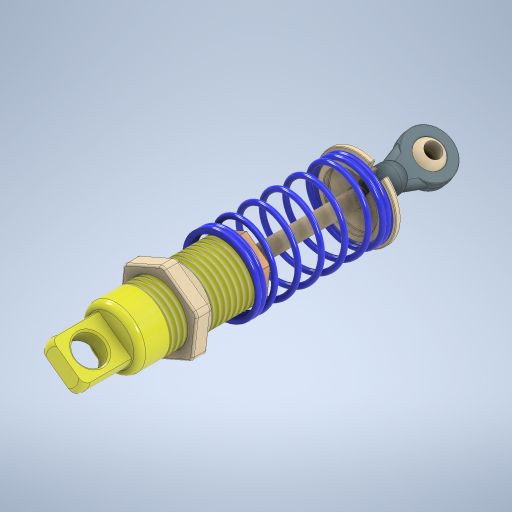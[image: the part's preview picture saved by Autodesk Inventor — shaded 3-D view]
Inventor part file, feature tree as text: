
AUTODESK INVENTOR PART (.ipt)
format: ipt  version: 2024 (Build 280153000, 153)  size: 2,274,816 bytes
history: native  units: in
note: dims shown in document units (in); Inventor stores cm internally (conversion verified against a paired STEP export)
features: other x16, plane x2, sketch x1
ambient origin geometry x8: Origin, YZ Plane, XZ Plane, XY Plane, X Axis, Y Axis, Z Axis, Center Point
bodies: Solid1 (feature_tree), Solid2 (feature_tree), Solid3 (feature_tree), Solid4 (feature_tree), Solid5 (feature_tree), Solid6 (feature_tree), Solid7 (feature_tree), Solid8 (feature_tree), Solid9 (feature_tree), Solid10 (feature_tree), Solid11 (feature_tree), Solid12 (feature_tree), Solid13 (feature_tree), Solid14 (feature_tree), Solid15 (feature_tree)
feature tree (19):
  other  "Shock Absorber Assembly.iam"
  other  "SA Shock Spring Adjustment Nut.ipt:1"
  other  "SA Suspension Spring.ipt:1"
  other  "Shock Body Assembly.iam:1::SA Shock Body.ipt:1"
  other  "Shock Body Assembly.iam:1::Shock Cartridge Assembly.iam:1::SA Shock Cartridge.ipt:1"
  other  "Shock Body Assembly.iam:1::Shock Cartridge Assembly.iam:1::SA O-Ring.ipt:1"
  other  "Shock Body Assembly.iam:1::Shock Cartridge Assembly.iam:1::SA Shock Cartridge Spacer.ipt:1"
  other  "Shock Body Assembly.iam:1::Shock Cartridge Assembly.iam:1::SA O-Ring.ipt:2"
  other  "Shock Body Assembly.iam:1::Shock Cartridge Assembly.iam:1::SA Shock Cardridge Cover.ipt:1"
  other  "Shock Strut Assembly.iam:1::SA Shock Shaft.ipt:1"
  other  "Shock Strut Assembly.iam:1::SA Piston.ipt:1"
  other  "Shock Strut Assembly.iam:1::SA E-Clip.ipt:1"
  other  "Shock Strut Assembly.iam:1::SA E-Clip.ipt:2"
  other  "Shock Strut Assembly.iam:1::Ball End Assembly.iam:1::SA Ball End.ipt:1"
  other  "Shock Strut Assembly.iam:1::Ball End Assembly.iam:1::SA Ball.ipt:1"
  other  "Shock Strut Assembly.iam:1::SA Spring Cup.ipt:1"
  plane  "Work Plane1"
  plane  "Work Plane2"
  sketch  "Sketch1"  dims[d0=3.937in]
